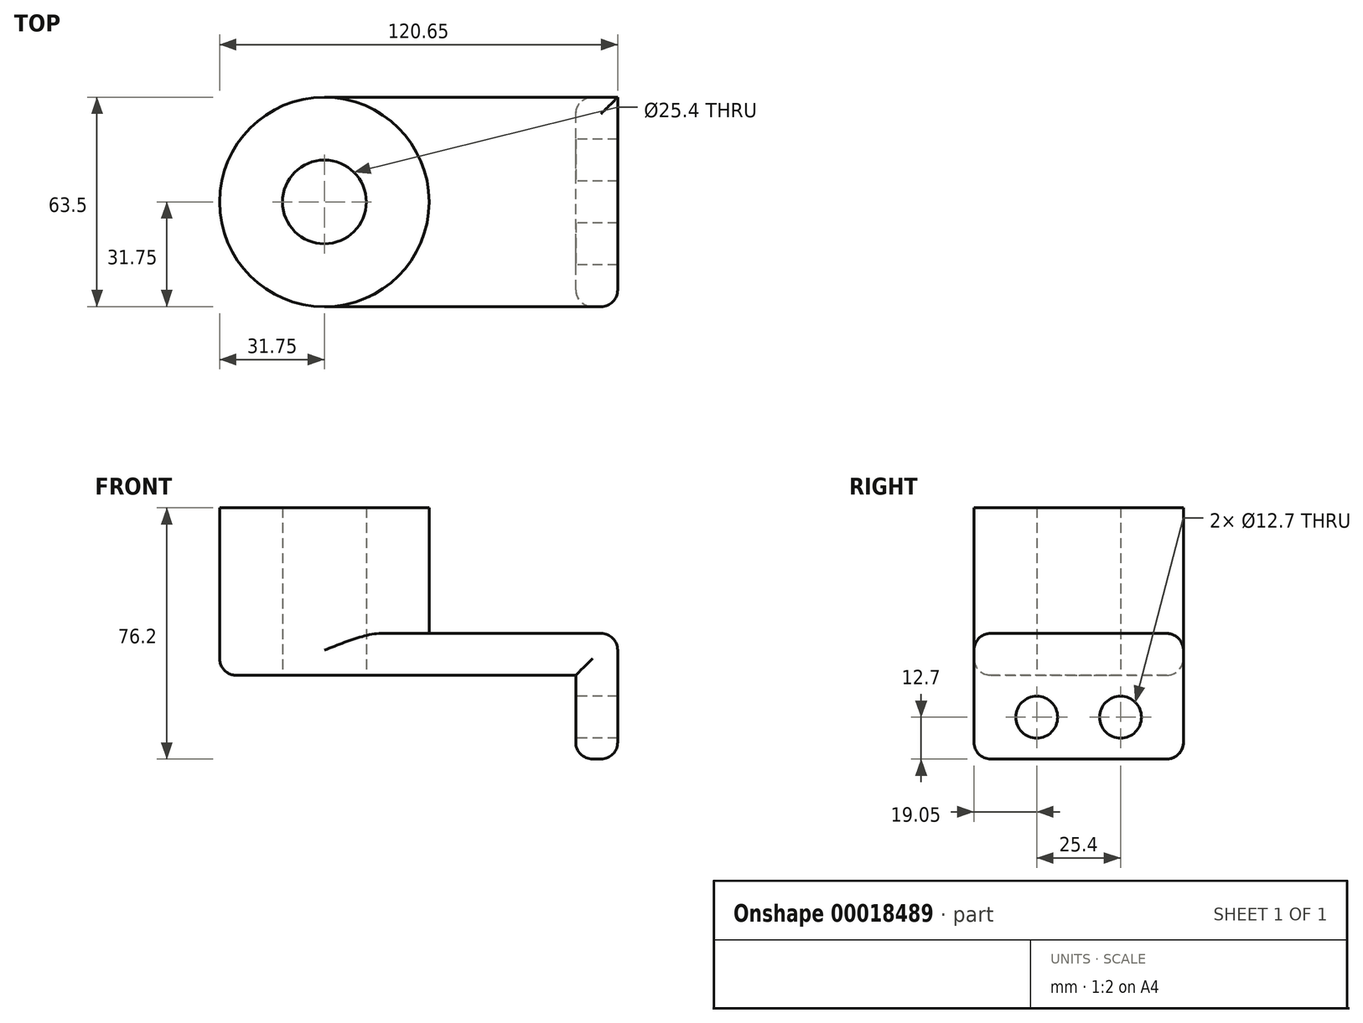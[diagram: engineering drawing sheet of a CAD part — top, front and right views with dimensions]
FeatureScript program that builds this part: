
annotation { "Feature Type Name" : "Feature", "Feature Type Description" : "" }
export const myFeature = defineFeature(function(context is Context, id is Id, definition is map)
    precondition{}
    {
        {
            var Q0;
            Q0=qCreatedBy(makeId("Top.planeOp"),FACE);
            var sketch = newSketch(context, id + "F0", { "sketchPlane" : qUnion([Q0])});
            skLineSegment(sketch, "E0.rect.bottom", {"start": v(38.1, -31.75) * mm, "end": v(-38.1, -31.75) * mm});
            skLineSegment(sketch, "E0.rect.top", {"start": v(38.1, 31.75) * mm, "end": v(-38.1, 31.75) * mm});
            skLineSegment(sketch, "E0.rect.left", {"start": v(38.1, -31.75) * mm, "end": v(38.1, 31.75) * mm});
            skLineSegment(sketch, "E0.rect.right", {"start": v(-38.1, -31.75) * mm, "end": v(-38.1, 31.75) * mm});
            skPoint(sketch, "E0.rect.middle", {"position": v(0, 0) * mm});
            skCircle(sketch, "E1", {"center": v(-38.1, 0) * mm, "radius": 31.75 * mm});
            skCircle(sketch, "E2", {"center": v(-38.1, 0) * mm, "radius": 12.7 * mm});
            skSolve(sketch);
        }
        {
            var Q0;
            {var subQ3=sQuery(id+"F0.wireOp",EDGE,"E0.rect.bottom");Q0=makeQuery(id+"F0.imprint","IMPRINT",FACE,{"disambiguationData":[TD([[makeQuery(id+"F0.imprint","IMPRINT",EDGE,{"derivedFrom":subQ3}),-1.0]])]});}
            var Q1;
            {var subQ0=sQuery(id+"F0.wireOp",EDGE,"E2");var subQ1=sQuery(id+"F0.wireOp",EDGE,"E0.rect.right");var subQ3=makeQuery(id+"F0.imprint","INTERSECT",VERTEX,{"disambiguationData":[OD(0.0)],"derivedFrom":[subQ1,subQ0]});Q1=makeQuery(id+"F0.imprint","IMPRINT",FACE,{"disambiguationData":[TD([[makeQuery(id+"F0.imprint","IMPRINT",EDGE,{"disambiguationData":[TD([[subQ3,1.0]])],"derivedFrom":subQ0}),-1.0]])]});}
            var Q2;
            {var subQ0=sQuery(id+"F0.wireOp",EDGE,"E2");var subQ1=sQuery(id+"F0.wireOp",EDGE,"E0.rect.right");var subQ3=makeQuery(id+"F0.imprint","INTERSECT",VERTEX,{"disambiguationData":[OD(0.0)],"derivedFrom":[subQ1,subQ0]});Q2=makeQuery(id+"F0.imprint","IMPRINT",FACE,{"disambiguationData":[TD([[makeQuery(id+"F0.imprint","IMPRINT",EDGE,{"disambiguationData":[TD([[subQ3,-1.0]])],"derivedFrom":subQ0}),-1.0]])]});}
            extrude(context, id + "F1", {"entities" : qUnion([Q0, Q1, Q2]), "depth" : 12.7 * mm});
        }
        {
            var Q0;
            {var subQ0=sQuery(id+"F0.wireOp",EDGE,"E2");var subQ1=sQuery(id+"F0.wireOp",EDGE,"E0.rect.right");var subQ3=makeQuery(id+"F0.imprint","INTERSECT",VERTEX,{"disambiguationData":[OD(0.0)],"derivedFrom":[subQ1,subQ0]});Q0=makeQuery(id+"F0.imprint","IMPRINT",FACE,{"disambiguationData":[TD([[makeQuery(id+"F0.imprint","IMPRINT",EDGE,{"disambiguationData":[TD([[subQ3,1.0]])],"derivedFrom":subQ0}),-1.0]])]});}
            var Q1;
            {var subQ0=sQuery(id+"F0.wireOp",EDGE,"E2");var subQ1=sQuery(id+"F0.wireOp",EDGE,"E0.rect.right");var subQ3=makeQuery(id+"F0.imprint","INTERSECT",VERTEX,{"disambiguationData":[OD(0.0)],"derivedFrom":[subQ1,subQ0]});Q1=makeQuery(id+"F0.imprint","IMPRINT",FACE,{"disambiguationData":[TD([[makeQuery(id+"F0.imprint","IMPRINT",EDGE,{"disambiguationData":[TD([[subQ3,-1.0]])],"derivedFrom":subQ0}),-1.0]])]});}
            extrude(context, id + "F2", {"entities" : qUnion([Q0, Q1]), "operationType" : NewBodyOperationType.ADD, "depth" : 50.8 * mm});
        }
        {
            var Q0;
            Q0=makeQuery(id+"F1.opExtrude","SWEPT_FACE",FACE,{"disambiguationData":[OSD([sQuery(id+"F0.wireOp",EDGE,"E0.rect.left")])]});
            var sketch = newSketch(context, id + "F3", { "sketchPlane" : qUnion([Q0])});
            skLineSegment(sketch, "E3.bottom", {"start": v(-31.75, 12.7) * mm, "end": v(31.75, 12.7) * mm});
            skLineSegment(sketch, "E3.top", {"start": v(-31.75, -25.4) * mm, "end": v(31.75, -25.4) * mm});
            skLineSegment(sketch, "E3.left", {"start": v(-31.75, 12.7) * mm, "end": v(-31.75, -25.4) * mm});
            skLineSegment(sketch, "E3.right", {"start": v(31.75, 12.7) * mm, "end": v(31.75, -25.4) * mm});
            skCircle(sketch, "E4", {"center": v(-12.7, -12.7) * mm, "radius": 6.35 * mm});
            skLineSegment(sketch, "E5", {"start": v(0, 0) * mm, "end": v(0, -25.4) * mm, "construction": true});
            skCircle(sketch, "E6.MirrorC", {"center": v(12.7, -12.7) * mm, "radius": 6.35 * mm, "construction": true});
            skCircle(sketch, "E7.MirrorC", {"center": v(-12.7, -12.7) * mm, "radius": 6.35 * mm, "construction": true});
            skCircle(sketch, "E8.MirrorC", {"center": v(12.7, -12.7) * mm, "radius": 6.35 * mm});
            skSolve(sketch);
        }
        {
            var Q0;
            Q0 = qSketchRegion(id + "F3", true);
            extrude(context, id + "F4", {"entities" : qUnion([Q0]), "operationType" : NewBodyOperationType.ADD, "depth" : 12.7 * mm});
        }
        {
            var Q0;
            Q0=makeQuery(id+"F4.boolean.opBoolean","MERGE",EDGE,{"derivedFrom":[makeQuery(id+"F1.opExtrude","CAP_EDGE",EDGE,{"disambiguationData":[OSD([sQuery(id+"F0.wireOp",EDGE,"E0.rect.bottom")])],"isStart":false}),makeQuery(id+"F4.opExtrude","SWEPT_EDGE",EDGE,{"disambiguationData":[OSD([sQuery(id+"F3.wireOp",EDGE,"E3.bottom"),sQuery(id+"F3.wireOp",EDGE,"E3.left")])]})]});
            var Q1;
            Q1=makeQuery(id+"F1.opExtrude","CAP_EDGE",EDGE,{"disambiguationData":[OSD([sQuery(id+"F0.wireOp",EDGE,"E0.rect.bottom")])],"isStart":true});
            var Q2;
            Q2=makeQuery(id+"F4.opExtrude","CAP_EDGE",EDGE,{"disambiguationData":[OSD([sQuery(id+"F3.wireOp",EDGE,"E3.left")])],"isStart":false});
            var Q3;
            Q3=makeQuery(id+"F4.opExtrude","CAP_EDGE",EDGE,{"disambiguationData":[OSD([sQuery(id+"F3.wireOp",EDGE,"E3.left")])],"isStart":true});
            var Q4;
            Q4=makeQuery(id+"F4.opExtrude","SWEPT_EDGE",EDGE,{"disambiguationData":[OSD([sQuery(id+"F3.wireOp",EDGE,"E3.top"),sQuery(id+"F3.wireOp",EDGE,"E3.left")])]});
            var Q5;
            Q5=makeQuery(id+"F4.opExtrude","CAP_EDGE",EDGE,{"disambiguationData":[OSD([sQuery(id+"F3.wireOp",EDGE,"E3.top")])],"isStart":false});
            var Q6;
            Q6=makeQuery(id+"F4.opExtrude","CAP_EDGE",EDGE,{"disambiguationData":[OSD([sQuery(id+"F3.wireOp",EDGE,"E3.bottom")])],"isStart":false});
            var Q7;
            Q7=makeQuery(id+"F4.boolean.opBoolean","MERGE",EDGE,{"derivedFrom":[makeQuery(id+"F1.opExtrude","CAP_EDGE",EDGE,{"disambiguationData":[OSD([sQuery(id+"F0.wireOp",EDGE,"E0.rect.top")])],"isStart":false}),makeQuery(id+"F4.opExtrude","SWEPT_EDGE",EDGE,{"disambiguationData":[OSD([sQuery(id+"F3.wireOp",EDGE,"E3.bottom"),sQuery(id+"F3.wireOp",EDGE,"E3.right")])]})]});
            var Q8;
            Q8=makeQuery(id+"F1.opExtrude","CAP_EDGE",EDGE,{"disambiguationData":[OSD([sQuery(id+"F0.wireOp",EDGE,"E0.rect.top")])],"isStart":true});
            var Q9;
            Q9=makeQuery(id+"F4.opExtrude","CAP_EDGE",EDGE,{"disambiguationData":[OSD([sQuery(id+"F3.wireOp",EDGE,"E3.right")])],"isStart":true});
            var Q10;
            Q10=makeQuery(id+"F4.opExtrude","SWEPT_EDGE",EDGE,{"disambiguationData":[OSD([sQuery(id+"F3.wireOp",EDGE,"E3.top"),sQuery(id+"F3.wireOp",EDGE,"E3.right")])]});
            var Q11;
            Q11=makeQuery(id+"F4.opExtrude","CAP_EDGE",EDGE,{"disambiguationData":[OSD([sQuery(id+"F3.wireOp",EDGE,"E3.top")])],"isStart":true});
            fillet(context, id + "F5", {"entities" : qUnion([Q0, Q1, Q2, Q3, Q4, Q5, Q6, Q7, Q8, Q9, Q10, Q11]), "radius" : 5.08 * mm, "tangentPropagation" : true, "allowEdgeOverflow" : false});
        }
    });
